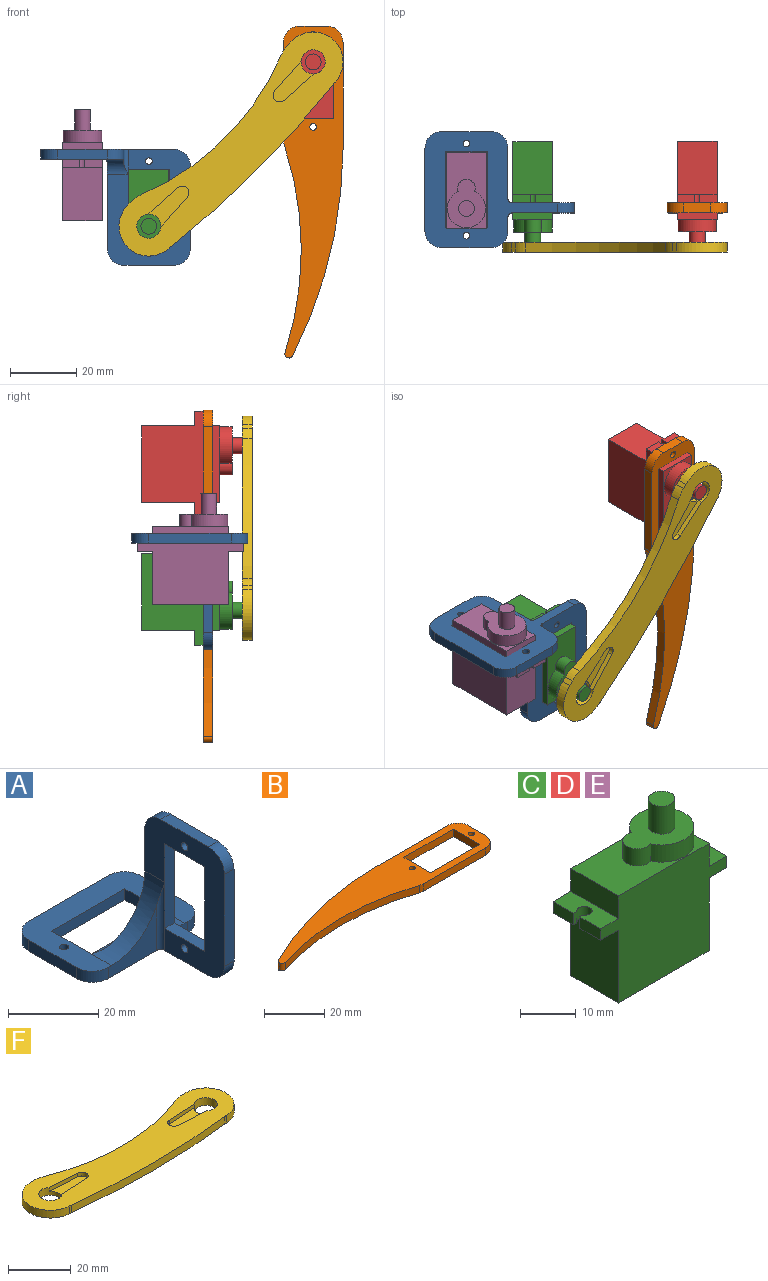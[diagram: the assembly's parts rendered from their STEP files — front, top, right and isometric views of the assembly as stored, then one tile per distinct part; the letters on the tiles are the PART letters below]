
ASSEMBLY  parts=6 mates=5
PART A: 36 faces, bbox 35x45x35 mm
  f0: plane 35x25mm, normal (1,0,0), area 518.2mm2, adj f14,f15,f16,f17,f18,f19,f20,f21
  f1: plane 35x25mm, normal (-1,0,0), area 449.5mm2, adj f14,f15,f16,f17,f18,f19,f20,f21
  f2: plane 4.39x4.25mm, normal (0,-1,0), area 14.1mm2, adj f13,f14,f27,f31,f35
  f3: plane 15x3mm, normal (1,0,0), area 45mm2, adj f13,f14,f27,f28
  f4: plane 25x3mm, normal (0,1,0), area 75mm2, adj f13,f14,f28,f29
  f5: plane 15x3mm, normal (-1,0,0), area 45mm2, adj f13,f14,f29,f30
  f6: plane 23x3mm, normal (0,1,0), area 69mm2, adj f7,f9,f14,f33
  f7: plane 12.5x3mm, normal (1,0,0), area 37.5mm2, adj f6,f8,f13,f14
  f8: plane 23x3mm, normal (0,-1,0), area 69mm2, adj f7,f9,f13,f14
  f9: plane 12.5x3mm, normal (-1,0,0), area 37.5mm2, adj f6,f8,f13,f14
  f10: cylinder r=1mm len=3mm, axis (0,0,-1), area 18.8mm2, adj f13,f14
  f11: cylinder r=1mm len=3mm, axis (0,0,-1), area 18.8mm2, adj f13,f14
  f12: plane 15.25x12.4mm, normal (0,-1,0), area 83.1mm2, adj f13,f14,f30,f32,f34
  f13: plane 35x25mm, normal (0,0,1), area 416mm2, adj f2,f3,f4,f5,f7,f8,f9,f10
  f14: plane 40x35mm, normal (0,0,-1), area 605.4mm2, adj f0,f1,f2,f3,f4,f5,f6,f7
  f15: plane 25.75x13.79mm, normal (0,1,0), area 116mm2, adj f0,f1,f26,f33,f34,f35
  f16: plane 25x3mm, normal (0,-1,0), area 75mm2, adj f0,f1,f24,f25
  f17: plane 15x3mm, normal (0,0,1), area 45mm2, adj f0,f1,f25,f26
  f18: plane 23x3mm, normal (0,-1,0), area 69mm2, adj f0,f1,f19,f21,f31,f32
  f19: plane 12.5x3mm, normal (0,0,-1), area 37.5mm2, adj f0,f1,f18,f20
  f20: plane 23x3mm, normal (0,1,0), area 69mm2, adj f0,f1,f19,f21
  f21: plane 12.5x3mm, normal (0,0,1), area 37.5mm2, adj f0,f1,f18,f20
  f22: cylinder r=1mm len=3mm, axis (1,0,0), area 18.8mm2, adj f0,f1
  f23: cylinder r=1mm len=3mm, axis (1,0,0), area 18.8mm2, adj f0,f1
  f24: cylinder r=5mm len=5mm, axis (1,0,0), area 23.6mm2, adj f0,f1,f14,f16
  f25: cylinder r=5mm len=5mm, axis (-1,0,0), area 23.6mm2, adj f0,f1,f16,f17
  f26: cylinder r=5mm len=5mm, axis (1,0,0), area 23.6mm2, adj f0,f1,f15,f17
  f27: cylinder r=5mm len=5mm, axis (0,0,1), area 23.6mm2, adj f2,f3,f13,f14
  f28: cylinder r=5mm len=5mm, axis (0,0,-1), area 23.6mm2, adj f3,f4,f13,f14
  f29: cylinder r=5mm len=5mm, axis (0,0,1), area 23.6mm2, adj f4,f5,f13,f14
  f30: cylinder r=5mm len=5mm, axis (0,0,-1), area 23.6mm2, adj f5,f12,f13,f14
  f31: cylinder r=1.25mm len=7.5mm, axis (0,0,-1), area 11.4mm2, adj f0,f2,f14,f18,f35
  f32: cylinder r=1.25mm len=18.5mm, axis (0,0,1), area 29.9mm2, adj f1,f12,f14,f18,f34
  f33: cylinder r=1.25mm len=23mm, axis (-1,0,0), area 35.4mm2, adj f6,f15,f34,f35
  f34: cylinder r=15.5mm len=15.5mm, axis (0,-1,0), area 127.8mm2, adj f1,f12,f13,f15,f32,f33
  f35: cylinder r=4.5mm len=7.5mm, axis (0,1,0), area 38.6mm2, adj f0,f2,f13,f15,f31,f33
PART B: 20 faces, bbox 100x18x3 mm
  f0: plane 23x3mm, normal (0,1,0), area 69mm2, adj f1,f11,f12,f13
  f1: plane 12.5x3mm, normal (1,0,0), area 37.5mm2, adj f0,f2,f12,f13
  f2: plane 23x3mm, normal (0,-1,0), area 69mm2, adj f1,f11,f12,f13
  f3: cylinder r=100mm len=62.62mm, axis (0,0,-1), area 191.1mm2, adj f12,f13,f14,f19
  f4: plane 29.18x3mm, normal (0,-1,0), area 87.5mm2, adj f12,f13,f14,f15
  f5: plane 8x3mm, normal (1,0,0), area 24mm2, adj f12,f13,f15,f16
  f6: plane 31.91x3mm, normal (0,1,0), area 95.7mm2, adj f12,f13,f16,f17
  f7: cylinder r=140mm len=62.38mm, axis (0,0,-1), area 194.3mm2, adj f12,f13,f17,f18
  f8: plane 3x0.02mm, normal (-1,0,0), area 0.1mm2, adj f12,f13,f18,f19
  f9: cylinder r=1mm len=3mm, axis (0,0,-1), area 18.8mm2, adj f12,f13
  f10: cylinder r=1mm len=3mm, axis (0,0,-1), area 18.8mm2, adj f12,f13
  f11: plane 12.5x3mm, normal (-1,0,0), area 37.5mm2, adj f0,f2,f12,f13
  f12: plane 100x18mm, normal (0,0,1), area 935.1mm2, adj f0,f1,f2,f3,f4,f5,f6,f7
  f13: plane 100x18mm, normal (0,0,-1), area 935.1mm2, adj f0,f1,f2,f3,f4,f5,f6,f7
  f14: cylinder r=5mm len=3mm, axis (0,0,-1), area 4.8mm2, adj f3,f4,f12,f13
  f15: cylinder r=5mm len=5mm, axis (0,0,1), area 23.6mm2, adj f4,f5,f12,f13
  f16: cylinder r=5mm len=5mm, axis (0,0,-1), area 23.6mm2, adj f5,f6,f12,f13
  f17: cylinder r=5mm len=3mm, axis (0,0,-1), area 0.1mm2, adj f6,f7,f12,f13
  f18: cylinder r=1.24mm len=3mm, axis (0,0,-1), area 4.1mm2, adj f7,f8,f12,f13
  f19: cylinder r=1.24mm len=3mm, axis (0,0,-1), area 7mm2, adj f3,f8,f12,f13
PART C: 27 faces, bbox 32x12x33.4 mm
  f0: plane 12x4.5mm, normal (0,0,1), area 47.1mm2, adj f3,f4,f5,f6,f7,f8,f9,f17
  f1: plane 12x4.5mm, normal (0,0,-1), area 47.1mm2, adj f3,f4,f5,f6,f7,f8,f9,f20
  f2: plane 5.25x2.5mm, normal (1,0,0), area 13.1mm2, adj f3,f13,f14,f15
  f3: plane 32x23.5mm, normal (0,1,0), area 563mm2, adj f0,f1,f2,f4,f14,f15,f16,f17
  f4: plane 5.25x2.5mm, normal (-1,0,0), area 13.1mm2, adj f0,f1,f3,f5
  f5: plane 2.5x0.78mm, normal (0,-1,0), area 1.9mm2, adj f0,f1,f4,f6
  f6: cylinder r=1.38mm len=2.75mm, axis (0,0,-1), area 17.6mm2, adj f0,f1,f5,f7
  f7: plane 2.5x0.78mm, normal (0,1,0), area 1.9mm2, adj f0,f1,f6,f8
  f8: plane 5.25x2.5mm, normal (-1,0,0), area 13.1mm2, adj f0,f1,f7,f9
  f9: plane 32x23.5mm, normal (0,-1,0), area 563mm2, adj f0,f1,f8,f10,f14,f15,f16,f17
  f10: plane 5.25x2.5mm, normal (1,0,0), area 13.1mm2, adj f9,f11,f14,f15
  f11: plane 2.5x1.17mm, normal (0,1,0), area 2.9mm2, adj f10,f12,f14,f15
  f12: cylinder r=1.38mm len=2.75mm, axis (0,0,-1), area 17.6mm2, adj f11,f13,f14,f15
  f13: plane 2.5x1.17mm, normal (0,-1,0), area 2.9mm2, adj f2,f12,f14,f15
  f14: plane 12x4.5mm, normal (0,0,1), area 46.5mm2, adj f2,f3,f9,f10,f11,f12,f13,f18
  f15: plane 12x4.5mm, normal (0,0,-1), area 46.5mm2, adj f2,f3,f9,f10,f11,f12,f13,f19
  f16: plane 23x12mm, normal (0,0,1), area 157.5mm2, adj f3,f9,f17,f18,f23,f24
  f17: plane 12x5mm, normal (-1,0,0), area 60mm2, adj f0,f3,f9,f16
  f18: plane 12x5mm, normal (1,0,0), area 60mm2, adj f3,f9,f14,f16
  f19: plane 16x12mm, normal (1,0,0), area 192mm2, adj f3,f9,f15,f21
  f20: plane 16x12mm, normal (-1,0,0), area 192mm2, adj f1,f3,f9,f21
  f21: plane 23x12mm, normal (0,0,-1), area 276mm2, adj f3,f9,f19,f20
  f22: plane 14.55x11.55mm, normal (0,0,1), area 100.8mm2, adj f23,f24,f25
  f23: cylinder r=5.77mm len=11.55mm, axis (0,0,-1), area 117mm2, adj f16,f22,f24
  f24: cylinder r=2.62mm len=5.25mm, axis (0,0,-1), area 38mm2, adj f16,f22,f23
  f25: cylinder r=2.38mm len=6.1mm, axis (0,0,-1), area 91mm2, adj f22,f26
  f26: plane 4.75x4.75mm, normal (0,0,1), area 17.7mm2, adj f25
PART D: same geometry as C
PART E: same geometry as C
PART F: 22 faces, bbox 88x20x3 mm
  f0: plane 12.01x1.5mm, normal (-0.06,1,0), area 18.1mm2, adj f1,f13,f14,f20
  f1: cylinder r=3.62mm len=7.25mm, axis (0,0,-1), area 59mm2, adj f0,f2,f14,f15,f20
  f2: plane 12.01x1.5mm, normal (-0.06,-1,0), area 18.1mm2, adj f1,f13,f14,f20
  f3: plane 3x1.51mm, normal (0,1,0), area 4.5mm2, adj f4,f14,f15,f17
  f4: cylinder r=9mm len=17.99mm, axis (0,0,-1), area 83.8mm2, adj f3,f14,f15,f18
  f5: cylinder r=300mm len=69.07mm, axis (0,0,-1), area 207.7mm2, adj f14,f15,f18,f19
  f6: cylinder r=9mm len=17.99mm, axis (0,0,-1), area 83.8mm2, adj f7,f14,f15,f19
  f7: plane 3x1.51mm, normal (0,1,0), area 4.5mm2, adj f6,f14,f15,f16
  f8: plane 12.01x1.5mm, normal (0.06,-1,0), area 18.1mm2, adj f9,f12,f14,f21
  f9: cylinder r=3.62mm len=7.25mm, axis (0,0,-1), area 59mm2, adj f8,f10,f14,f15,f21
  f10: plane 12.01x1.5mm, normal (0.06,1,0), area 18.1mm2, adj f9,f12,f14,f21
  f11: cylinder r=80mm len=59.54mm, axis (0,0,-1), area 183mm2, adj f14,f15,f16,f17
  f12: cylinder r=2mm len=3.99mm, axis (0,0,-1), area 9mm2, adj f8,f10,f14,f21
  f13: cylinder r=2mm len=3.99mm, axis (0,0,-1), area 9mm2, adj f0,f2,f14,f20
  f14: plane 88x20.05mm, normal (0,0,1), area 1137.4mm2, adj f0,f1,f2,f3,f4,f5,f6,f7
  f15: plane 88x20.05mm, normal (0,0,-1), area 1253.4mm2, adj f1,f3,f4,f5,f6,f7,f9,f11
  f16: cylinder r=10mm len=3.72mm, axis (0,0,-1), area 11.4mm2, adj f7,f11,f14,f15
  f17: cylinder r=10mm len=3.72mm, axis (0,0,-1), area 11.4mm2, adj f3,f11,f14,f15
  f18: cylinder r=10mm len=3mm, axis (0,0,1), area 2.4mm2, adj f4,f5,f14,f15
  f19: cylinder r=10mm len=3mm, axis (0,0,1), area 2.4mm2, adj f5,f6,f14,f15
  f20: plane 13.89x5.5mm, normal (0,0,1), area 58mm2, adj f0,f1,f2,f13
  f21: plane 13.89x5.5mm, normal (0,0,1), area 58mm2, adj f8,f9,f10,f12
PLACE A rot(axis=(-0.71,0.71,0),180deg) t=(2.33,-16.12,-0.21)mm
PLACE B rot(axis=(-0.58,-0.58,-0.58),120deg) t=(71.83,-23.12,-13.11)mm
PLACE C rot(axis=(0.58,0.58,-0.58),120deg) t=(22.33,-17.62,-17.71)mm
PLACE D rot(axis=(0.58,-0.58,0.58),120deg) t=(71.83,-17.62,20.39)mm
PLACE E rot(axis=(0,0,-1),90deg) t=(2.33,-16.12,-5.71)mm
PLACE F rot(axis=(0.86,-0.36,0.36),98.4deg) t=(47.08,-31.97,1.34)mm
MATE fastened B.f9 <-> D.f12  axis (0,1,0) through (71.83,-20.12,34.26)mm
MATE fastened A.f11 <-> E.f6  axis (0,0,1) through (2.33,-2.24,-3.21)mm
MATE fastened C.f6 <-> A.f23  axis (0,1,0) through (22.33,-20.12,-3.84)mm
MATE revolute F.f6 <-> D.f23  axis (0,-1,0) through (71.83,-34.97,26.09)mm
MATE revolute C.f23 <-> F.f1  axis (0,-1,0) through (22.33,-34.97,-23.41)mm
